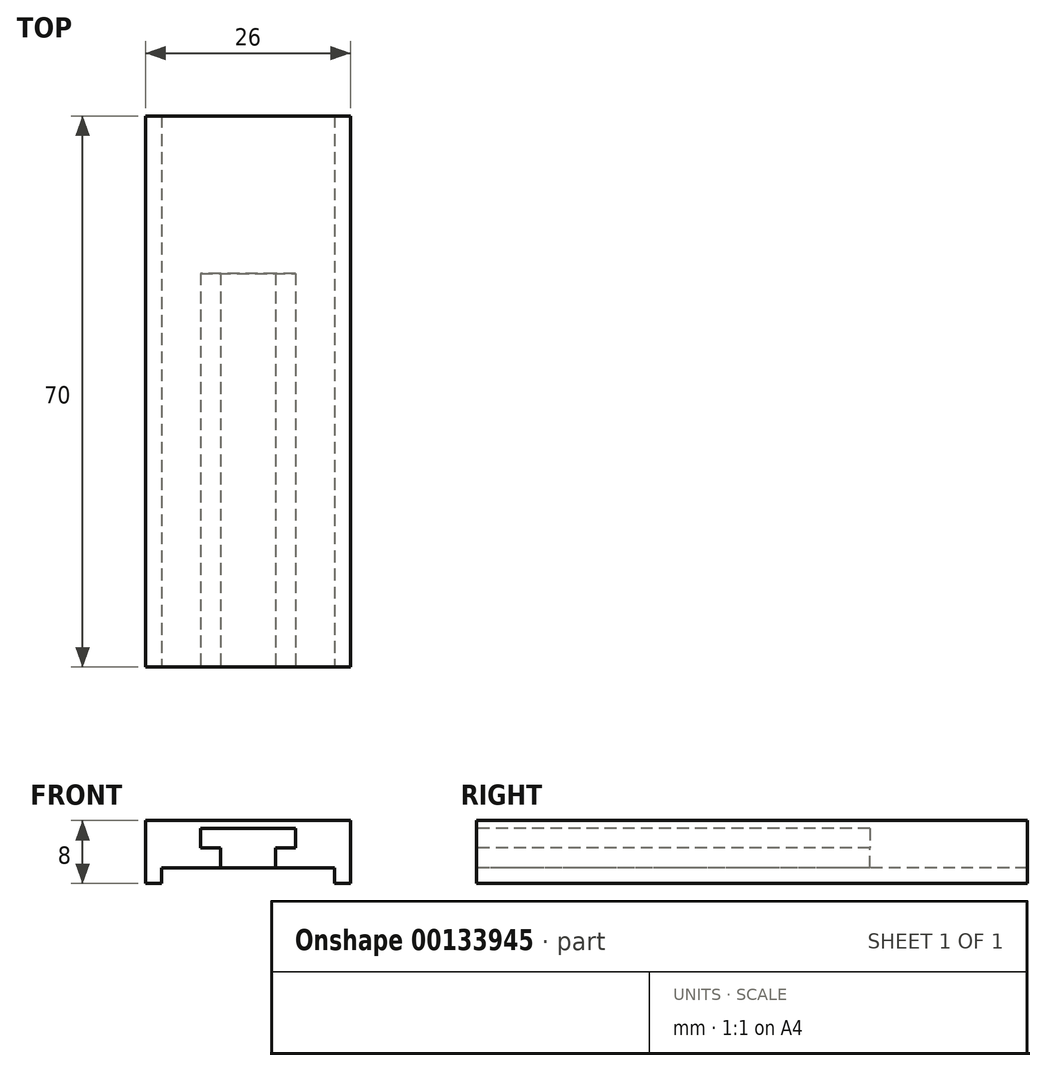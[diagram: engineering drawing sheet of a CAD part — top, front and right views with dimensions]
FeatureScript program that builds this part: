
annotation { "Feature Type Name" : "Feature", "Feature Type Description" : "" }
export const myFeature = defineFeature(function(context is Context, id is Id, definition is map)
    precondition{}
    {
        {
            var Q0;
            Q0=qCreatedBy(makeId("Front.planeOp"),FACE);
            var sketch = newSketch(context, id + "F0", { "sketchPlane" : qUnion([Q0])});
            skLineSegment(sketch, "E0.bottom", {"start": v(11, -6) * mm, "end": v(-11, -6) * mm});
            skPoint(sketch, "E0.middle", {"position": v(0, 0) * mm});
            skLineSegment(sketch, "E1", {"start": v(13, 0) * mm, "end": v(-13, 0) * mm});
            skLineSegment(sketch, "E2", {"start": v(-13, 0) * mm, "end": v(-13, -8) * mm});
            skLineSegment(sketch, "E3", {"start": v(-13, -8) * mm, "end": v(-11, -8) * mm});
            skLineSegment(sketch, "E4", {"start": v(-11, -8) * mm, "end": v(-11, -6) * mm});
            skLineSegment(sketch, "E5", {"start": v(13, 0) * mm, "end": v(13, -8) * mm});
            skLineSegment(sketch, "E6", {"start": v(13, -8) * mm, "end": v(11, -8) * mm});
            skLineSegment(sketch, "E7", {"start": v(11, -8) * mm, "end": v(11, -6) * mm});
            skSolve(sketch);
        }
        {
            var Q0;
            Q0=qSketchRegion(id+"F0",true);
            extrude(context, id + "F1", {"entities" : qUnion([Q0]), "oppositeDirection" : true, "depth" : 70 * mm});
        }
        {
            var Q0;
            Q0=makeQuery(id+"F1.opExtrude","CAP_FACE",FACE,{"disambiguationData":[OSD([sQuery(id+"F0.wireOp",EDGE,"E0.bottom"),sQuery(id+"F0.wireOp",EDGE,"E0.top"),sQuery(id+"F0.wireOp",EDGE,"E0.left"),sQuery(id+"F0.wireOp",EDGE,"E0.right")])],"isStart":true});
            var sketch = newSketch(context, id + "F2", { "sketchPlane" : qUnion([Q0])});
            skLineSegment(sketch, "E8", {"start": v(-3.5, -6) * mm, "end": v(-3.5, -3.5) * mm});
            skLineSegment(sketch, "E9", {"start": v(-3.5, -3.5) * mm, "end": v(-6, -3.5) * mm});
            skLineSegment(sketch, "E10", {"start": v(-6, -3.5) * mm, "end": v(-6, -1) * mm});
            skLineSegment(sketch, "E11", {"start": v(-6, -1) * mm, "end": v(6, -1) * mm});
            skLineSegment(sketch, "E12", {"start": v(6, -1) * mm, "end": v(6, -3.5) * mm});
            skLineSegment(sketch, "E13", {"start": v(6, -3.5) * mm, "end": v(3.5, -3.5) * mm});
            skLineSegment(sketch, "E14", {"start": v(3.5, -3.5) * mm, "end": v(3.5, -6) * mm});
            skLineSegment(sketch, "E15", {"start": v(-3.5, -6) * mm, "end": v(3.5, -6) * mm});
            skSolve(sketch);
        }
        {
            var Q0;
            Q0=qSketchRegion(id+"F2",true);
            extrude(context, id + "F3", {"entities" : qUnion([Q0]), "operationType" : NewBodyOperationType.REMOVE, "oppositeDirection" : true, "depth" : 50 * mm});
        }
    });
